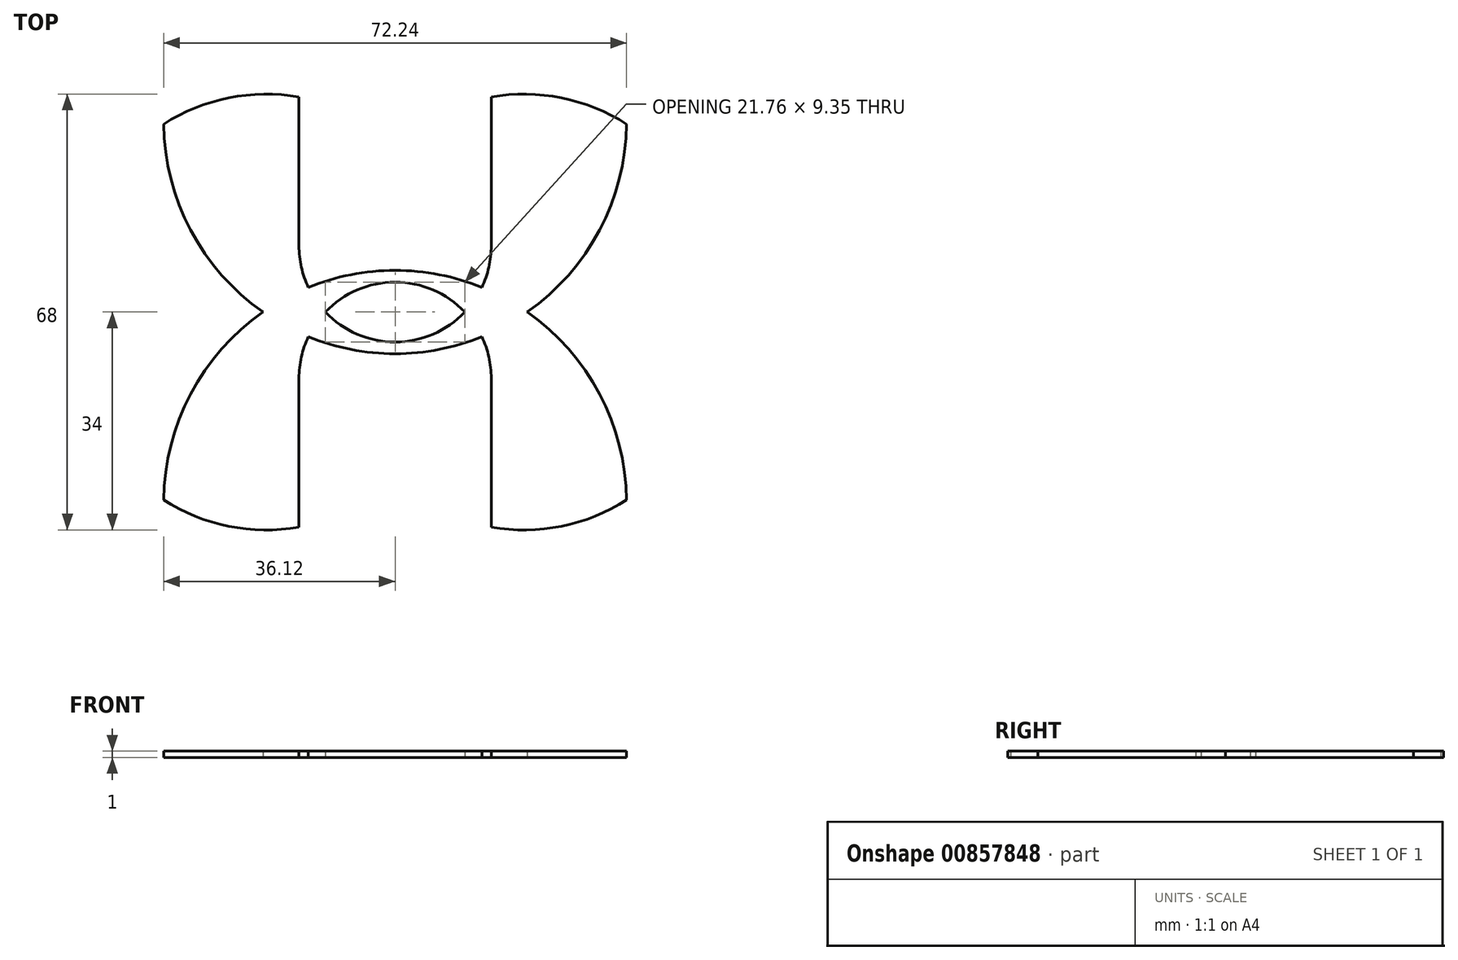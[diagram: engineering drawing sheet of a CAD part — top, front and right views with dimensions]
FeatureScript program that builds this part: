
annotation { "Feature Type Name" : "Feature", "Feature Type Description" : "" }
export const myFeature = defineFeature(function(context is Context, id is Id, definition is map)
    precondition{}
    {
        {
            var Q0;
            Q0=qCreatedBy(makeId("Top.planeOp"),FACE);
            var sketch = newSketch(context, id + "F0", { "sketchPlane" : qUnion([Q0])});
            skLineSegment(sketch, "E0", {"start": v(-15, 33.57) * mm, "end": v(-15, 10.33) * mm});
            skArc(sketch, "E1", {"start": v(-15, 10.33) * mm, "mid": v(-14.63, 7) * mm, "end": v(-13.53, 3.84) * mm});
            skArc(sketch, "E2", {"start": v(-36.12, 29.32) * mm, "mid": v(-31.91, 12.78) * mm, "end": v(-20.6, 0) * mm});
            skArc(sketch, "E3", {"start": v(-15, 33.57) * mm, "mid": v(-25.96, 33.42) * mm, "end": v(-36.12, 29.32) * mm});
            skLineSegment(sketch, "E4.MirrorCS", {"start": v(15, 33.57) * mm, "end": v(15, 10.33) * mm});
            skArc(sketch, "E5.MirrorCS", {"start": v(15, 33.57) * mm, "mid": v(25.96, 33.42) * mm, "end": v(36.12, 29.32) * mm});
            skArc(sketch, "E6.MirrorCS", {"start": v(36.12, 29.32) * mm, "mid": v(31.91, 12.78) * mm, "end": v(20.6, 0) * mm});
            skArc(sketch, "E7.MirrorCS", {"start": v(15, 10.33) * mm, "mid": v(14.63, 7) * mm, "end": v(13.53, 3.84) * mm});
            skArc(sketch, "E8.MirrorCS", {"start": v(36.12, -29.32) * mm, "mid": v(31.91, -12.78) * mm, "end": v(20.6, 0) * mm});
            skLineSegment(sketch, "E9.MirrorCS", {"start": v(15, -33.57) * mm, "end": v(15, -10.33) * mm});
            skArc(sketch, "E10.MirrorCS", {"start": v(15, -10.33) * mm, "mid": v(14.63, -7) * mm, "end": v(13.53, -3.84) * mm});
            skArc(sketch, "E11.MirrorCS", {"start": v(15, -33.57) * mm, "mid": v(25.96, -33.42) * mm, "end": v(36.12, -29.32) * mm});
            skLineSegment(sketch, "E12.MirrorCS", {"start": v(-15, -33.57) * mm, "end": v(-15, -10.33) * mm});
            skArc(sketch, "E13.MirrorCS", {"start": v(-15, -33.57) * mm, "mid": v(-25.96, -33.42) * mm, "end": v(-36.12, -29.32) * mm});
            skArc(sketch, "E14.MirrorCS", {"start": v(-36.12, -29.32) * mm, "mid": v(-31.91, -12.78) * mm, "end": v(-20.6, 0) * mm});
            skArc(sketch, "E15.MirrorCS", {"start": v(-15, -10.33) * mm, "mid": v(-14.63, -7) * mm, "end": v(-13.53, -3.84) * mm});
            skArc(sketch, "E16.trimOffspring", {"start": v(10.88, 0) * mm, "mid": v(5.92, 3.46) * mm, "end": v(0, 4.67) * mm});
            skArc(sketch, "E17.trimOffspring", {"start": v(13.53, 3.84) * mm, "mid": v(6.9, 5.83) * mm, "end": v(0, 6.52) * mm});
            skArc(sketch, "E18.trimOffspring", {"start": v(-10.88, 0) * mm, "mid": v(-5.92, -3.46) * mm, "end": v(0, -4.67) * mm});
            skArc(sketch, "E19.trimOffspring", {"start": v(-13.53, -3.84) * mm, "mid": v(-6.9, -5.83) * mm, "end": v(0, -6.52) * mm});
            skArc(sketch, "E20.trimOffspring", {"start": v(10.88, 0) * mm, "mid": v(5.92, -3.46) * mm, "end": v(0, -4.67) * mm});
            skArc(sketch, "E21.trimOffspring", {"start": v(13.53, -3.84) * mm, "mid": v(6.9, -5.83) * mm, "end": v(0, -6.52) * mm});
            skArc(sketch, "E22.trimOffspring", {"start": v(-10.88, 0) * mm, "mid": v(-5.92, 3.46) * mm, "end": v(0, 4.67) * mm});
            skArc(sketch, "E23.trimOffspring", {"start": v(-13.53, 3.84) * mm, "mid": v(-6.9, 5.83) * mm, "end": v(0, 6.52) * mm});
            skSolve(sketch);
        }
        {
            var Q0;
            Q0=makeQuery(id+"F0.imprint","IMPRINT",FACE,{"disambiguationData":[TD([[makeQuery(id+"F0.imprint","IMPRINT",EDGE,{"derivedFrom":sQuery(id+"F0.wireOp",EDGE,"E0")}),-1.0]])]});
            extrude(context, id + "F1", {"entities" : qUnion([Q0]), "depth" : 1 * mm, "offsetDistance" : 25 * mm});
        }
    });
